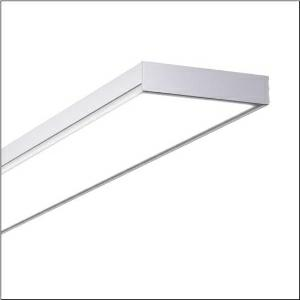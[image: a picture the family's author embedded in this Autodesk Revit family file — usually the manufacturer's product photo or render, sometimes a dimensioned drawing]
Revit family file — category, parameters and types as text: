
# Revit family: apollon_r__31_surface_51mp25wd2441ea_850e
name_source: partatom
category: Lighting Fixtures
units: mm (PartAtom-declared; Revit-internal decimal feet)

## family parameters
Cut with Voids When Loaded = No
Host = Face
Light Source = No
Part Type = Normal
Room Calculation Point = No
Round Connector Dimension = Use Diameter
Shared = No

## types (1)
- Apollon® 31 Surface (1 x LED, 3800 lm, 28 W, 4000K)
    Apparent Load = 28 VA
    CIE Flux Codes = 61 87 97 97 100
    Color Rendering = 80
    Color Temperature = 4000K
    Default Elevation = 1800 mm
    Description = Apollon® 31 Surface, office luminaire, primary optical cover: micro prismatic cover, of PMMA, light emission: direct distribution, primary light characteristic: symmetric, installation type: surface-mounted, LED, rated luminous flux: 3.800lm, luminous efficacy: 134lm/W, light colour: 840, colour temperature: 4000K, control gear: DALI 2, with terminal, 5-pole, mains connection: 220..240V, AC, 50/60Hz, rated input power: 28W, housing, of sheet steel, coil coated, metallic grey (RAL 9006), length: 1.245mm, width: 200mm, height: 44mm, protection rating (complete): IP20, insulation class (complete): insulation class II (safety insulation), certification: CE, impact resistance: IK02, permissible operating ambient temperature: -20..+40°C, standard: EN 60598-2-22, packaging unit: 1 piece
    Height = 44 mm
    Lamp = 1 x LED
    Lamp Light Flux = 3800 lm
    Lamp Power = 28 W
    Lamp count = 1
    Length = 1245 mm
    Luminous efficacy = 136 lm/W
    Manufacturer = Siteco
    ModVariant = No
    Model = 51MP25WD2441EA
    Mounting Place = Ceiling
    Mounting Type = Surface mounted
    Number of Poles = 1
    OnlyDefault = Yes
    Power Factor = 1
    Product Name = Apollon® 31 Surface
    Product group = office luminaire | ceiling mounted
    ProductGroupID = 303
    Protection Class = Protection class II
    Protection Degree = IP 20
    RLX_Detail_Level = 1
    RLX_Emergency_Light_Flux = 0 lm
    RLX_Emergency_Type = 0
    RLX_Emergency_Type_DB = No
    RlxData = <blob elided: 24105 chars, md5=b4a3f780>
    Socket = socket
    Standby Power = 0 W
    System Light Flux = 3800 lm
    System Power = 28 W
    Type Comments = Product without accessories
    Type Image = l_1313654.jpg
    URL = http://relux.com
    VarID = ---
    Voltage = 0 V
    Weight = 0.00 kg
    Width = 200 mm

## geometry (parser evidence)
native form markers: Blend x4, Sweep x9
no freeform markers — native parametric forms only
